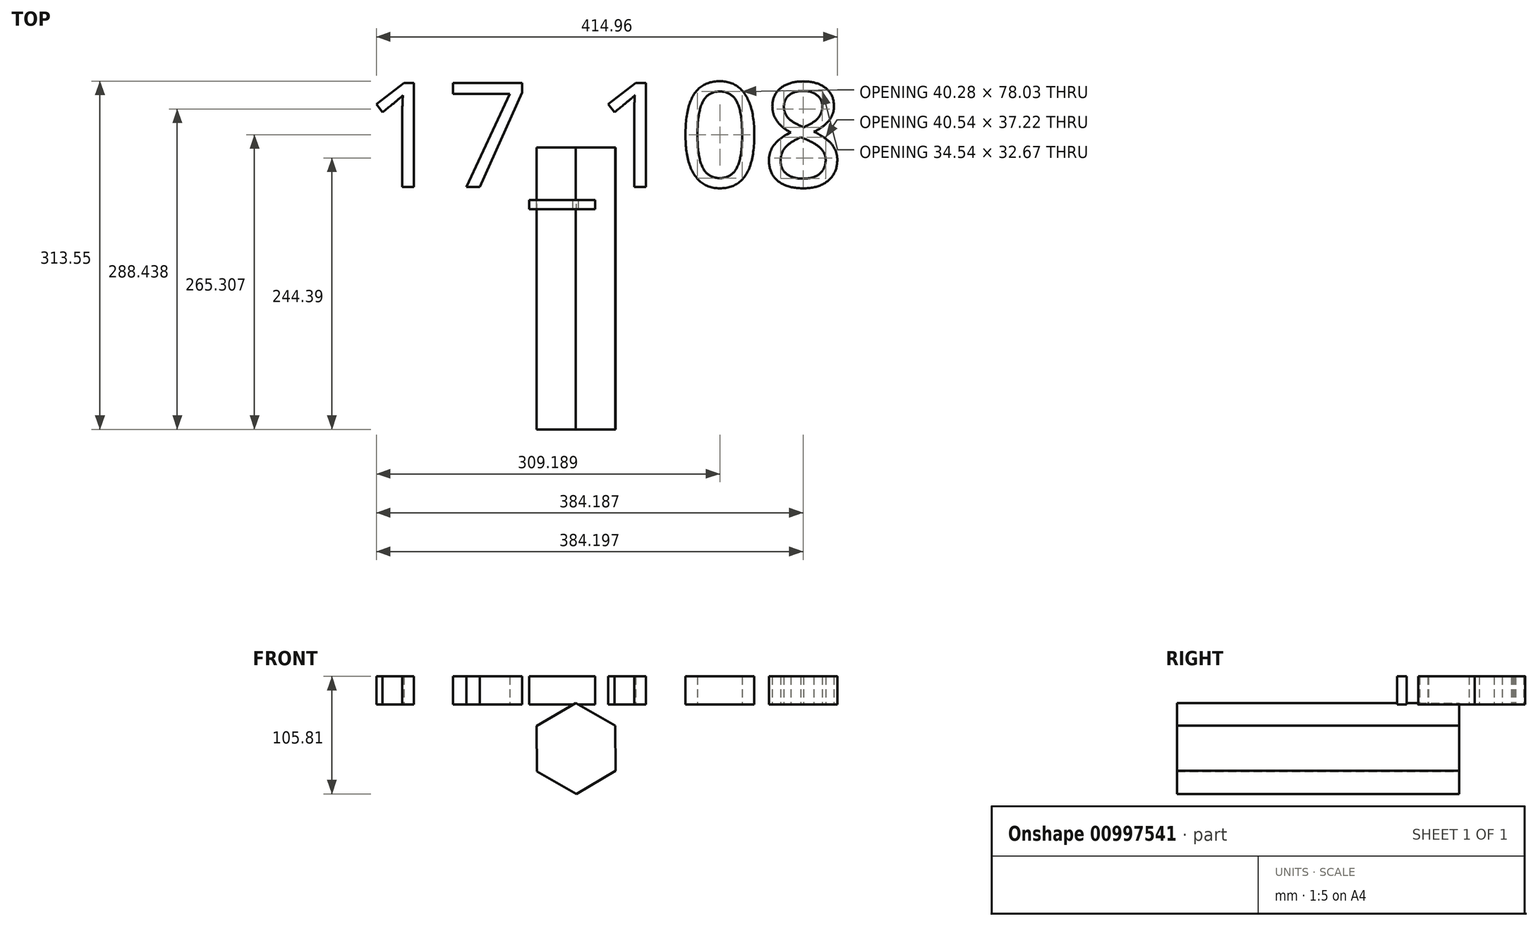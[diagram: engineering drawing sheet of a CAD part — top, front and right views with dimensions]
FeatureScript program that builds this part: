
annotation { "Feature Type Name" : "Feature", "Feature Type Description" : "" }
export const myFeature = defineFeature(function(context is Context, id is Id, definition is map)
    precondition{}
    {
        {
            var Q0;
            Q0=qCreatedBy(makeId("Front.planeOp"),FACE);
            var sketch = newSketch(context, id + "F0", { "sketchPlane" : qUnion([Q0])});
            skCircle(sketch, "E0.cCircle", {"center": v(38.53, 30.45) * mm, "radius": 37.65 * mm, "construction": true});
            skLineSegment(sketch, "E0.0", {"start": v(37.87, -13.02) * mm, "end": v(0.55, 9.28) * mm});
            skLineSegment(sketch, "E0.1", {"start": v(0.55, 9.28) * mm, "end": v(1.2, 52.75) * mm});
            skLineSegment(sketch, "E0.2", {"start": v(1.2, 52.75) * mm, "end": v(39.18, 73.92) * mm});
            skLineSegment(sketch, "E0.3", {"start": v(39.18, 73.92) * mm, "end": v(76.5, 51.62) * mm});
            skLineSegment(sketch, "E0.4", {"start": v(76.5, 51.62) * mm, "end": v(75.85, 8.15) * mm});
            skLineSegment(sketch, "E0.5", {"start": v(75.85, 8.15) * mm, "end": v(37.87, -13.02) * mm});
            skPoint(sketch, "E0.0.midPoint", {"position": v(19.21, -1.87) * mm});
            skCircle(sketch, "E1.cCircle", {"center": v(-40.7, -39.51) * mm, "radius": 35.42 * mm, "construction": true});
            skLineSegment(sketch, "E1.0", {"start": v(-5.13, -59.7) * mm, "end": v(-40.4, -80.41) * mm});
            skLineSegment(sketch, "E1.1", {"start": v(-40.4, -80.41) * mm, "end": v(-75.97, -60.22) * mm});
            skLineSegment(sketch, "E1.2", {"start": v(-75.97, -60.22) * mm, "end": v(-76.26, -19.32) * mm});
            skLineSegment(sketch, "E1.3", {"start": v(-76.26, -19.32) * mm, "end": v(-41, 1.39) * mm});
            skLineSegment(sketch, "E1.4", {"start": v(-41, 1.39) * mm, "end": v(-5.42, -18.8) * mm});
            skLineSegment(sketch, "E1.5", {"start": v(-5.42, -18.8) * mm, "end": v(-5.13, -59.7) * mm});
            skPoint(sketch, "E1.0.midPoint", {"position": v(-22.76, -70.06) * mm});
            skCircle(sketch, "E2.cCircle", {"center": v(37.94, -36.56) * mm, "radius": 37.45 * mm, "construction": true});
            skLineSegment(sketch, "E2.0", {"start": v(39.24, 5) * mm, "end": v(71.24, -11.67) * mm});
            skLineSegment(sketch, "E2.1", {"start": v(71.24, -11.67) * mm, "end": v(78.15, -47.08) * mm});
            skLineSegment(sketch, "E2.2", {"start": v(78.15, -47.08) * mm, "end": v(54.78, -74.56) * mm});
            skLineSegment(sketch, "E2.3", {"start": v(54.78, -74.56) * mm, "end": v(18.73, -73.42) * mm});
            skLineSegment(sketch, "E2.4", {"start": v(18.73, -73.42) * mm, "end": v(-2.86, -44.53) * mm});
            skLineSegment(sketch, "E2.5", {"start": v(-2.86, -44.53) * mm, "end": v(6.27, -9.63) * mm});
            skLineSegment(sketch, "E2.6", {"start": v(6.27, -9.63) * mm, "end": v(39.24, 5) * mm});
            skPoint(sketch, "E2.0.midPoint", {"position": v(55.24, -3.34) * mm});
            skCircle(sketch, "E3.cCircle", {"center": v(62.18, -5.42) * mm, "radius": 11.79 * mm, "construction": true});
            skLineSegment(sketch, "E3.0", {"start": v(54.87, -15.2) * mm, "end": v(50.96, -10.23) * mm});
            skLineSegment(sketch, "E3.1", {"start": v(50.96, -10.23) * mm, "end": v(50.06, -3.98) * mm});
            skLineSegment(sketch, "E3.2", {"start": v(50.06, -3.98) * mm, "end": v(52.4, 1.89) * mm});
            skLineSegment(sketch, "E3.3", {"start": v(52.4, 1.89) * mm, "end": v(57.37, 5.8) * mm});
            skLineSegment(sketch, "E3.4", {"start": v(57.37, 5.8) * mm, "end": v(63.62, 6.7) * mm});
            skLineSegment(sketch, "E3.5", {"start": v(63.62, 6.7) * mm, "end": v(69.48, 4.35) * mm});
            skLineSegment(sketch, "E3.6", {"start": v(69.48, 4.35) * mm, "end": v(73.4, -0.6) * mm});
            skLineSegment(sketch, "E3.7", {"start": v(73.4, -0.6) * mm, "end": v(74.3, -6.86) * mm});
            skLineSegment(sketch, "E3.8", {"start": v(74.3, -6.86) * mm, "end": v(71.95, -12.73) * mm});
            skLineSegment(sketch, "E3.9", {"start": v(71.95, -12.73) * mm, "end": v(66.99, -16.64) * mm});
            skLineSegment(sketch, "E3.10", {"start": v(66.99, -16.64) * mm, "end": v(60.73, -17.54) * mm});
            skLineSegment(sketch, "E3.11", {"start": v(60.73, -17.54) * mm, "end": v(54.87, -15.2) * mm});
            skPoint(sketch, "E3.0.midPoint", {"position": v(52.91, -12.71) * mm});
            skSolve(sketch);
        }
        {
            var Q0;
            Q0 = qSketchRegion(id + "F0", true);
            extrude(context, id + "F1", {"entities" : qUnion([Q0]), "depth" : 254 * mm, "offsetDistance" : 25.4 * mm});
        }
        {
            var Q0;
            Q0=makeQuery(id+"F1.opExtrude","SWEPT_BODY",BODY,{"disambiguationData":[OSD([sQuery(id+"F0.wireOp",EDGE,"E0.0"),sQuery(id+"F0.wireOp",EDGE,"E0.1"),sQuery(id+"F0.wireOp",EDGE,"E0.2"),sQuery(id+"F0.wireOp",EDGE,"E0.3"),sQuery(id+"F0.wireOp",EDGE,"E0.4"),sQuery(id+"F0.wireOp",EDGE,"E0.5"),sQuery(id+"F0.wireOp",EDGE,"E2.0"),sQuery(id+"F0.wireOp",EDGE,"E2.1"),sQuery(id+"F0.wireOp",EDGE,"E2.2"),sQuery(id+"F0.wireOp",EDGE,"E2.3"),sQuery(id+"F0.wireOp",EDGE,"E2.4"),sQuery(id+"F0.wireOp",EDGE,"E2.5"),sQuery(id+"F0.wireOp",EDGE,"E2.6"),sQuery(id+"F0.wireOp",EDGE,"E3.1"),sQuery(id+"F0.wireOp",EDGE,"E3.2"),sQuery(id+"F0.wireOp",EDGE,"E3.5"),sQuery(id+"F0.wireOp",EDGE,"E3.6"),sQuery(id+"F0.wireOp",EDGE,"E3.7"),sQuery(id+"F0.wireOp",EDGE,"E3.8"),sQuery(id+"F0.wireOp",EDGE,"E3.9")])]});
            deleteBodies(context, id + "F2", {"entities" : qUnion([Q0])});
        }
        {
            var Q0;
            Q0=qCreatedBy(makeId("Top.planeOp"),FACE);
            var sketch = newSketch(context, id + "F3", { "sketchPlane" : qUnion([Q0])});
            skText(sketch, "E4", { "text": "17_108", "fontName": "OpenSans-Regular.ttf"});
            const initialGuessF3  = {"E4": [-0.23242, -0.03558, 1, 0, 0.09445]};
            skSetInitialGuess(sketch, initialGuessF3);
            skSolve(sketch);
        }
        {
            var Q0;
            Q0 = qSketchRegion(id + "F3", true);
            extrude(context, id + "F4", {"entities" : qUnion([Q0]), "operationType" : NewBodyOperationType.ADD, "depth" : 25.4 * mm, "offsetDistance" : 25.4 * mm});
        }
    });
